# Revit family: Resideo_UnderFloorMultiZoneController_HCC100
name_source: partatom
category: Electrical Fixtures
units: mm (PartAtom-declared; Revit-internal decimal feet)

## family parameters
Cut with Voids When Loaded = No
Host = Face
Maintain Annotation Orientation = No
OmniClass Number = 23.75.65.11.11
OmniClass Title = Heating Controllers
Part Type = Normal
Room Calculation Point = No
Round Connector Dimension = Use Diameter
Shared = No

## types (1)
- HCC100
    Accessory1 = MT4 Thermo-electric actuator, Normally closed, Closing dimension 11.0 mm [MT4-230-NC-HCC]
    Accessory2 = MT4 Thermo-electric actuator, Normally open, Closing dimension 11.0 mm [MT4-230-NO-HCC]
    Accessory3 = Condensation switch [EE046-T11]
    Actuator1-20 = 20 x 230 V AC/0,5 A (1A inrush) TRIAC (actuator) outputs
    AmbientRelativeHumidity(NonCondensing) = 0 .. 90%
    AmbientTemperature = 0 .. 40°C
    Antenna = Module with SMA connector and 2 m coaxial cable
    Application = Wired and/or wireless multi-zone underfloor heating or cooling control with on/off or OpenTherm appliance control and Evohome compatible
    ApprovalsAndStandards = 2014/35/EU and 2014/53/EU, Environmental: RoHS; WEEE; CE; UKCA
    Assembly Code = D3060
    AssetType = Fixed
    BIMObjectName = Resideo_UnderFloorMultiZoneController_HCC100
    Bluetooth[2.4GHz] = Max Power 100mW, 2.4–2.458GHz
    CableCrossSection = Maximum 2.5 mm2
    CableLength = Maximum 100m
    Cascade = Option for multiple controllers (max. 3 controllers)
    ClassificationName = Uniclass2015
    ClassificationValue = Pr_75_50_18_17
    Color = White
    Configuration = Via Bluetooth® with Resideo Pro app
    Cost = 0 $
    Default Elevation = 0 mm  [stored 0 ft]
    Description = UNDER-FLOOR HEATING CONTROLLER
    DocumentationCertificates = https://www.bimstore.co
    DocumentationInstallationGuide = https://www.bimstore.co
    DocumentationLiterature = https://www.bimstore.co
    DocumentationMaintenance = https://www.bimstore.co
    DocumentationTechnical = https://www.bimstore.co
    DurationUnit = Year
    ErPClass = VIII
    ExpectedLife = 0
    Features = • 6 wired temperature-controlled zones with (OpenTherm®) thermostats
• Up to 8 wireless temperature-controlled zones with Honeywell Home wireless thermostats
• 20 freely configurable thermoelectric actuators outputs
• Controller status LED indications on cover
• Fast installation, no screws used for wired terminals (except for power and pump)
• Integrated 230 V pump relay
• Heat demand control
– OpenTherm®
– Integrated potential free relay contact (230 V)
• Cool demand control
– OpenTherm®
– Integrated potential free relay contact (230 V)
• Heat/cool changeover options
– OpenTherm® command leading zone thermostat
– OpenTherm® command from OpenTherm® appliance
– Integrated potential free relay contact (230 V)
– Integrated heat/cool changeover input (On/Off)
• Patented Self-learning (Fuzzy Logic) algorithm for accurate zone temperature control
• Intelligent thermo-actuator output control to improve energy efficiency of the system
• Antenna module with 2 m cable for optimal signal strength
• Evohome zone control integration
• Option for wireless demand and/or heat/cool changeover relay module
• Installer Resideo Pro app for simplified configuration
    Heat/CoolDemand = SPST relay 24-230 V AC/1 A
    Heat/CoolModeChangeoverInput = Digital switch input
    HumiditySwitchInput = Digital switch input
    IPClass = IP30
    IfcExportAs = IfcUnitaryControlElement
    IfcExportType = IfcUnitaryControlElementTypeEnum.CONTROLPANEL
    Includes = Controller, antenna module, 230V power cable with EU plug, assembly bag with plugs and screws
    Keynote = W
    Manufacturer = Resideo
    ManufacturerName = Resideo
    Model = HCC100
    ModelNumber = HCC100
    ModelReference = HCC100 - Underfloor Multi-zone Controller
    MountingType = DIN-rail, Wall Mounted
    NBSDescription = Control panel
    NBSObjectName = Resideo - Control panel
    NominalDepth = 118 mm
    NominalHeight = 57 mm
    NominalLength = 330 mm
    NumberOfOutputs = 20 free configurable 230V/0,5A outputs
    NumberOfZones = 6 wired and up to 8 with wireless
    OpenTherm®Output = OpenTherm® V4.1A
    OutdoorSensor = 20K NTC sensor
    OuterDiameter = Minimum 8.0 mm, maximum 11 mm
    PowerSupply = 230 V AC + 10 - 15 %, 50 Hz Maximum power 7 VA (controller only) Fuse 3.15 A
    PrimaryMaterial = Resideo - Plastic - White
    ProductDimensions = 118mm (D) x 57mm (H) x 330mm (L)
    ProductionYear = 2022
    Pump = 230 V AC/1 A powered output
    RadioFrequency[868MHz] = Receiver Category 2, Max RF Power 25mW, 868–868.6MHz (868.3MHz)
    ReferencedStandard = 2014/35/EU and 2014/53/EU, Environmental: RoHS; WEEE; CE; UKCA
    Size = 118mm (D) x 57mm (H) x 330mm (L)
    StrippingLength = 7 mm
    SupplyWaterSensor = 20K NTC sensor
    TerminalRangeOfConnectors = 0.20–2.50 mm2: flexible/fixed connection; 0.50–1.50 mm2: flexible, with wire end ferrule
    Type Comments = HCC100 - Underfloor Multi-zone Controller
    TypeName = HCC100 - Underfloor Multi-zone Controller
    URL = https://www.resideo.com
    WarrantyDurationLabor = 0
    WarrantyDurationParts = 0
    WarrantyDurationUnit = Year
    WarrantyGuarantorLabor = https://www.resideo.com
    WarrantyGuarantorParts = https://www.resideo.com
    Zone1-6 = Wired OpenTherm® Zone Thermostats
    _BSBibleVersion = 17
    _BimSpecGuid = 0
    _CurrentRevision = 1
    _DistributedBy = https://www.bimstore.co
    _ObjectUserGuide = https://www.bimstore.co

note: [stored X ft] marks values corroborated as IEEE doubles in the binary element streams (Revit-internal decimal feet)

## geometry (parser evidence)
native form markers: Sweep x2
no freeform markers — native parametric forms only
